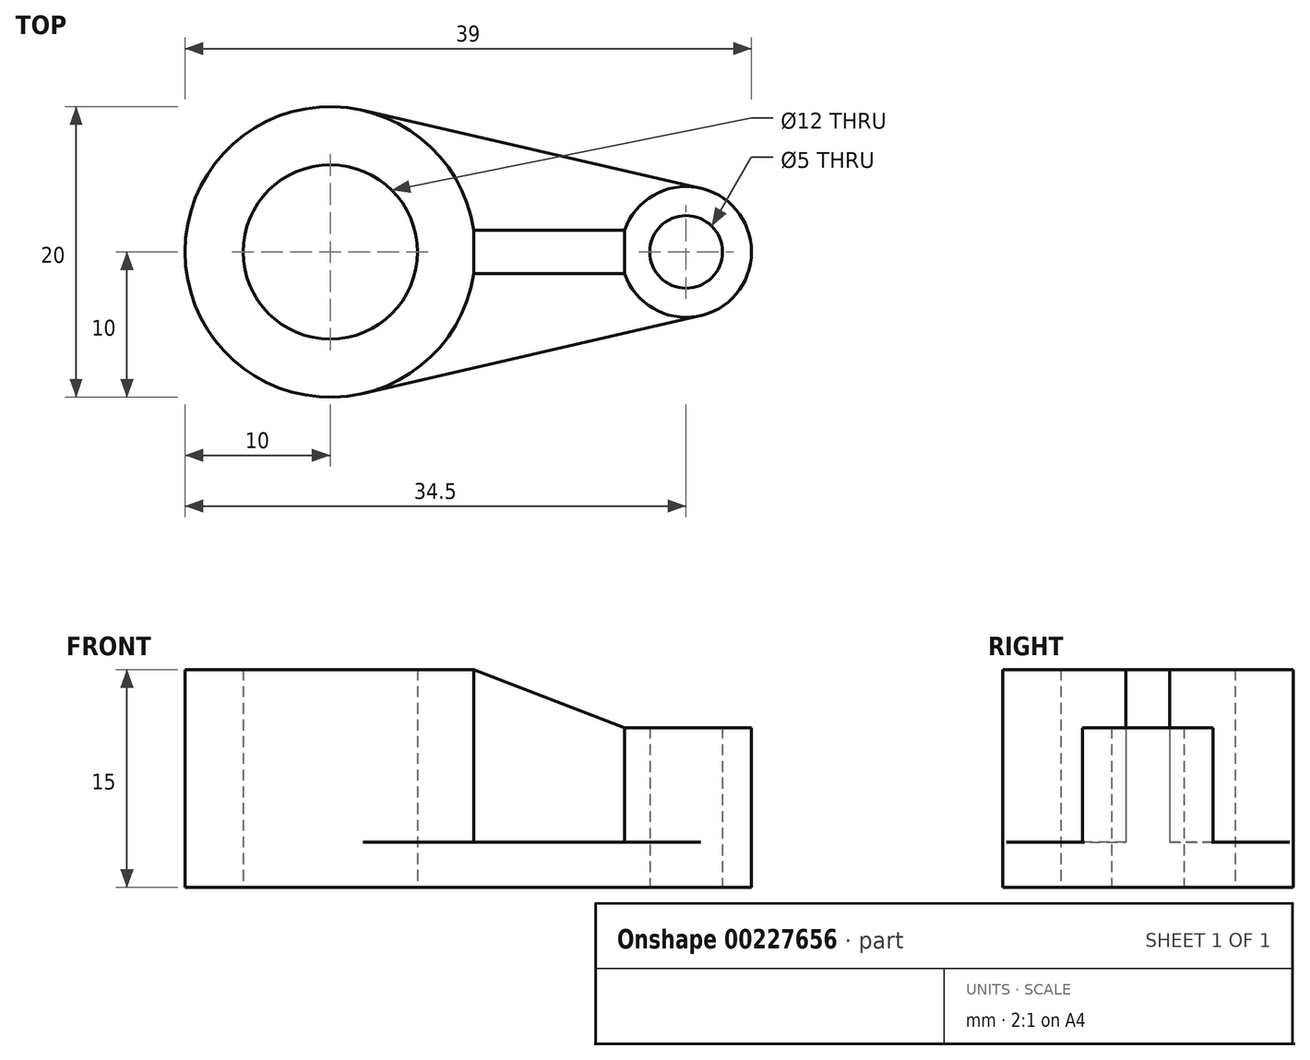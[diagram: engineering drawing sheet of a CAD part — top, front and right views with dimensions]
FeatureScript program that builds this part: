
annotation { "Feature Type Name" : "Feature", "Feature Type Description" : "" }
export const myFeature = defineFeature(function(context is Context, id is Id, definition is map)
    precondition{}
    {
        {
            var Q0;
            Q0=qCreatedBy(makeId("Top.planeOp"),FACE);
            var sketch = newSketch(context, id + "F0", { "sketchPlane" : qUnion([Q0])});
            skCircle(sketch, "E0", {"center": v(0, 0) * mm, "radius": 10 * mm});
            skCircle(sketch, "E1", {"center": v(0, 0) * mm, "radius": 6 * mm});
            skLineSegment(sketch, "E2", {"start": v(-21.73, 0) * mm, "end": v(46.76, 0) * mm, "construction": true});
            skCircle(sketch, "E3", {"center": v(24.5, 0) * mm, "radius": 4.5 * mm});
            skCircle(sketch, "E4", {"center": v(24.5, 0) * mm, "radius": 2.5 * mm});
            skLineSegment(sketch, "E5", {"start": v(25.51, -4.39) * mm, "end": v(2.24, -9.74) * mm});
            skLineSegment(sketch, "E6", {"start": v(25.51, 4.39) * mm, "end": v(2.24, 9.74) * mm});
            skLineSegment(sketch, "E7", {"start": v(5.8, 1.5) * mm, "end": v(22.5, 1.5) * mm});
            skLineSegment(sketch, "E8", {"start": v(5.8, -1.5) * mm, "end": v(22.5, -1.5) * mm});
            skSolve(sketch);
        }
        {
            var Q0;
            {var subQ5=sQuery(id+"F0.wireOp",EDGE,"E0");var subQ8=makeQuery(id+"F0.imprint","INTERSECT",VERTEX,{"derivedFrom":[subQ5,sQuery(id+"F0.wireOp",EDGE,"E6")]});Q0=makeQuery(id+"F0.imprint","IMPRINT",FACE,{"disambiguationData":[TD([[makeQuery(id+"F0.imprint","IMPRINT",EDGE,{"disambiguationData":[TD([[subQ8,1.0]])],"derivedFrom":subQ5}),1.0]])]});}
            var Q1;
            {var subQ0=sQuery(id+"F0.wireOp",EDGE,"E7");var subQ1=sQuery(id+"F0.wireOp",EDGE,"E0");var subQ2=makeQuery(id+"F0.imprint","INTERSECT",VERTEX,{"derivedFrom":[subQ1,subQ0]});Q1=makeQuery(id+"F0.imprint","IMPRINT",FACE,{"disambiguationData":[TD([[makeQuery(id+"F0.imprint","IMPRINT",EDGE,{"disambiguationData":[TD([[subQ2,1.0]])],"derivedFrom":subQ1}),1.0]])]});}
            extrude(context, id + "F1", {"entities" : qUnion([Q0, Q1]), "depth" : 15 * mm});
        }
        {
            var Q0;
            {var subQ0=sQuery(id+"F0.wireOp",EDGE,"E7");var subQ1=sQuery(id+"F0.wireOp",EDGE,"E0");var subQ2=makeQuery(id+"F0.imprint","INTERSECT",VERTEX,{"derivedFrom":[subQ1,subQ0]});Q0=makeQuery(id+"F0.imprint","IMPRINT",FACE,{"disambiguationData":[TD([[makeQuery(id+"F0.imprint","IMPRINT",EDGE,{"disambiguationData":[TD([[subQ2,1.0]])],"derivedFrom":subQ1}),-1.0]])]});}
            var Q1;
            {var subQ0=sQuery(id+"F0.wireOp",EDGE,"E7");var subQ1=sQuery(id+"F0.wireOp",EDGE,"E3");var subQ2=makeQuery(id+"F0.imprint","INTERSECT",VERTEX,{"derivedFrom":[subQ1,subQ0]});Q1=makeQuery(id+"F0.imprint","IMPRINT",FACE,{"disambiguationData":[TD([[makeQuery(id+"F0.imprint","IMPRINT",EDGE,{"disambiguationData":[TD([[subQ2,-1.0]])],"derivedFrom":subQ1}),1.0]])]});}
            extrude(context, id + "F2", {"entities" : qUnion([Q0, Q1]), "operationType" : NewBodyOperationType.ADD, "depth" : 15 * mm});
        }
        {
            var Q0;
            {var subQ5=sQuery(id+"F0.wireOp",EDGE,"E3");var subQ7=makeQuery(id+"F0.imprint","INTERSECT",VERTEX,{"derivedFrom":[subQ5,sQuery(id+"F0.wireOp",EDGE,"E6")]});Q0=makeQuery(id+"F0.imprint","IMPRINT",FACE,{"disambiguationData":[TD([[makeQuery(id+"F0.imprint","IMPRINT",EDGE,{"disambiguationData":[TD([[subQ7,-1.0]])],"derivedFrom":subQ5}),1.0]])]});}
            extrude(context, id + "F3", {"entities" : qUnion([Q0]), "operationType" : NewBodyOperationType.ADD, "depth" : 11 * mm});
        }
        {
            var Q0;
            {var subQ0=sQuery(id+"F0.wireOp",EDGE,"E5");Q0=makeQuery(id+"F0.imprint","IMPRINT",FACE,{"disambiguationData":[TD([[makeQuery(id+"F0.imprint","IMPRINT",EDGE,{"derivedFrom":subQ0}),-1.0]])]});}
            var Q1;
            {var subQ0=sQuery(id+"F0.wireOp",EDGE,"E6");Q1=makeQuery(id+"F0.imprint","IMPRINT",FACE,{"disambiguationData":[TD([[makeQuery(id+"F0.imprint","IMPRINT",EDGE,{"derivedFrom":subQ0}),1.0]])]});}
            extrude(context, id + "F4", {"entities" : qUnion([Q0, Q1]), "operationType" : NewBodyOperationType.ADD, "depth" : 3.1 * mm});
        }
        {
            var Q0;
            Q0=makeQuery(id+"F2.opExtrude","SWEPT_FACE",FACE,{"disambiguationData":[OSD([sQuery(id+"F0.wireOp",EDGE,"E8")])]});
            var sketch = newSketch(context, id + "F5", { "sketchPlane" : qUnion([Q0])});
            skPoint(sketch, "E9.0", {"position": v(20.26, 11) * mm});
            skPoint(sketch, "E10.0", {"position": v(9.89, 15) * mm});
            skLineSegment(sketch, "E11.0", {"start": v(9.89, 15) * mm, "end": v(22.5, 15) * mm});
            skLineSegment(sketch, "E12.0", {"start": v(22.5, 15) * mm, "end": v(22.5, 11) * mm});
            skLineSegment(sketch, "E13.0", {"start": v(20.26, 11) * mm, "end": v(22.5, 11) * mm});
            skPoint(sketch, "E14.orphan", {"position": v(29, 11) * mm});
            skLineSegment(sketch, "E15", {"start": v(20.26, 11) * mm, "end": v(9.89, 15) * mm});
            skSolve(sketch);
        }
        {
            var Q0;
            Q0=makeQuery(id+"F5.imprint","IMPRINT",FACE,{"disambiguationData":[TD([[makeQuery(id+"F5.imprint","IMPRINT",EDGE,{"derivedFrom":sQuery(id+"F5.wireOp",EDGE,"E11.0")}),-1.0]])]});
            extrude(context, id + "F6", {"entities" : qUnion([Q0]), "operationType" : NewBodyOperationType.REMOVE, "endBound" : BoundingType.UP_TO_NEXT, "oppositeDirection" : true, "depth" : 25 * mm});
        }
    });
